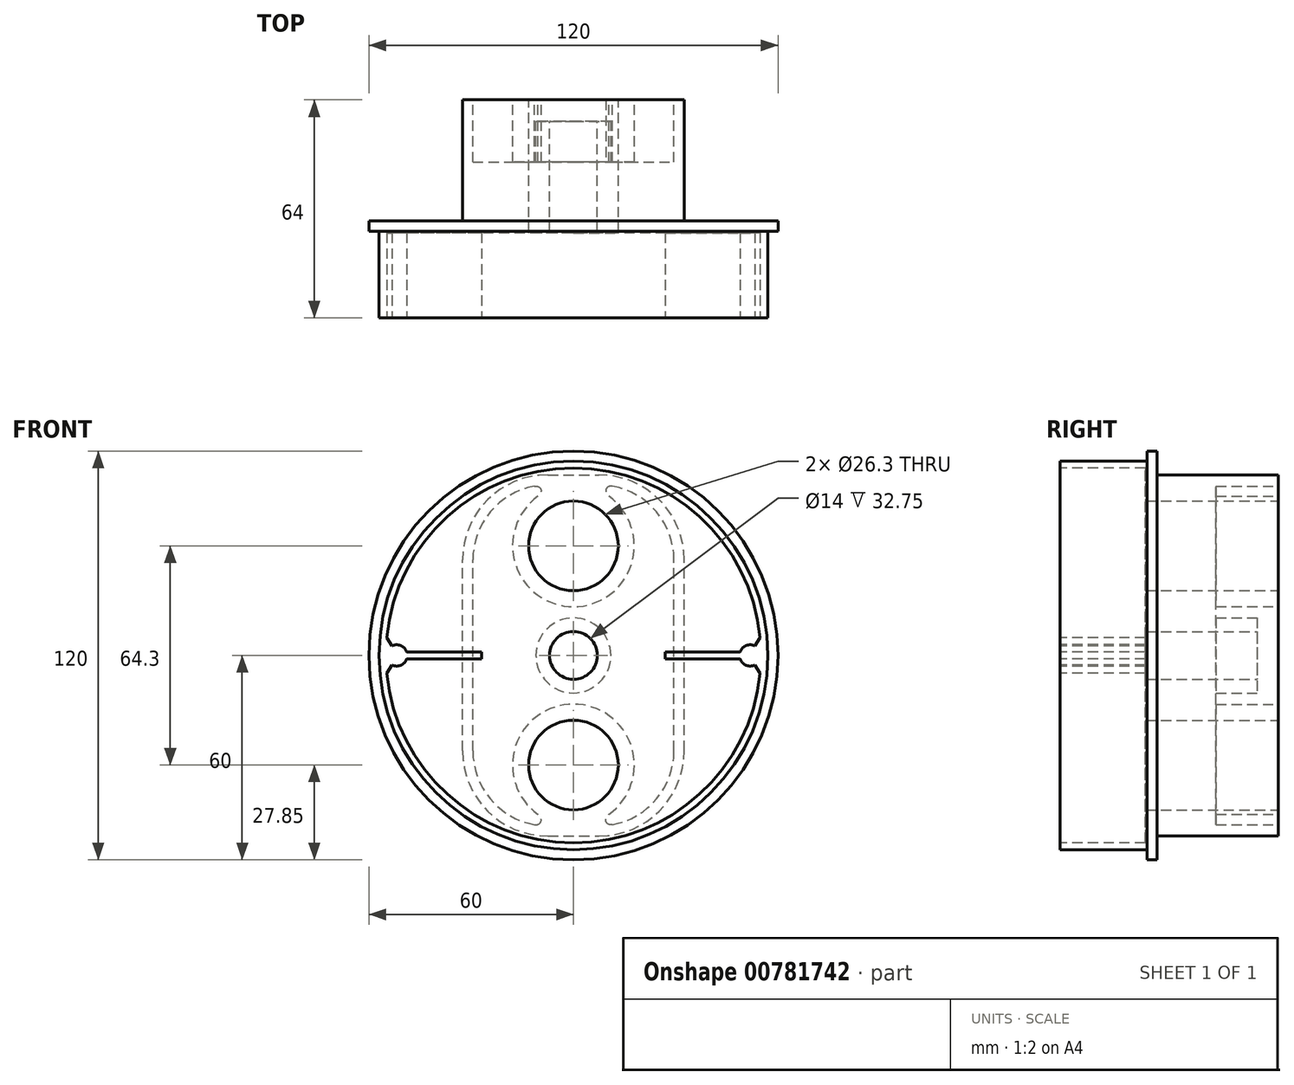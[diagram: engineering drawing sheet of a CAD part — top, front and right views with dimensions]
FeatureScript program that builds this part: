
annotation { "Feature Type Name" : "Feature", "Feature Type Description" : "" }
export const myFeature = defineFeature(function(context is Context, id is Id, definition is map)
    precondition{}
    {
        {
            var Q0;
            Q0=qCreatedBy(makeId("Front.planeOp"),FACE);
            var sketch = newSketch(context, id + "F0", { "sketchPlane" : qUnion([Q0])});
            skLineSegment(sketch, "E0.bottom", {"start": v(-7.5, -53) * mm, "end": v(7.5, -53) * mm});
            skLineSegment(sketch, "E0.top", {"start": v(-7.5, 53) * mm, "end": v(7.5, 53) * mm});
            skLineSegment(sketch, "E0.left", {"start": v(-32.5, -28) * mm, "end": v(-32.5, 28) * mm});
            skLineSegment(sketch, "E0.right", {"start": v(32.5, -28) * mm, "end": v(32.5, 28) * mm});
            skPoint(sketch, "E0.middle", {"position": v(0, 0) * mm});
            skPoint(sketch, "E1.visualSharp", {"position": v(32.5, 53) * mm});
            skArc(sketch, "E1.filletArc", {"start": v(32.5, 28) * mm, "mid": v(25.18, 45.68) * mm, "end": v(7.5, 53) * mm});
            skPoint(sketch, "E2.visualSharp", {"position": v(-32.5, 53) * mm});
            skArc(sketch, "E2.filletArc", {"start": v(-7.5, 53) * mm, "mid": v(-25.18, 45.68) * mm, "end": v(-32.5, 28) * mm});
            skPoint(sketch, "E3.visualSharp", {"position": v(32.5, -53) * mm});
            skArc(sketch, "E3.filletArc", {"start": v(7.5, -53) * mm, "mid": v(25.18, -45.68) * mm, "end": v(32.5, -28) * mm});
            skPoint(sketch, "E4.visualSharp", {"position": v(-32.5, -53) * mm});
            skArc(sketch, "E4.filletArc", {"start": v(-32.5, -28) * mm, "mid": v(-25.18, -45.68) * mm, "end": v(-7.5, -53) * mm});
            skSolve(sketch);
        }
        {
            var Q0;
            Q0 = qSketchRegion(id + "F0", true);
            extrude(context, id + "F1", {"entities" : qUnion([Q0]), "depth" : 64 * mm, "offsetDistance" : 25 * mm});
        }
        {
            var Q0;
            Q0=makeQuery(id+"F1.opExtrude","CAP_FACE",FACE,{"disambiguationData":[OSD([sQuery(id+"F0.wireOp",EDGE,"E0.bottom"),sQuery(id+"F0.wireOp",EDGE,"E0.top"),sQuery(id+"F0.wireOp",EDGE,"E0.left"),sQuery(id+"F0.wireOp",EDGE,"E0.right"),sQuery(id+"F0.wireOp",EDGE,"E1.filletArc"),sQuery(id+"F0.wireOp",EDGE,"E2.filletArc"),sQuery(id+"F0.wireOp",EDGE,"E3.filletArc"),sQuery(id+"F0.wireOp",EDGE,"E4.filletArc")])],"isStart":false});
            var sketch = newSketch(context, id + "F2", { "sketchPlane" : qUnion([Q0])});
            skCircle(sketch, "E5", {"center": v(0, 0) * mm, "radius": 60 * mm});
            skSolve(sketch);
        }
        {
            var Q0;
            Q0 = qSketchRegion(id + "F2", true);
            extrude(context, id + "F3", {"entities" : qUnion([Q0]), "operationType" : NewBodyOperationType.ADD, "oppositeDirection" : true, "depth" : 28.5 * mm, "offsetDistance" : 25 * mm});
        }
        {
            var Q0;
            Q0=makeQuery(id+"F3.boolean.opBoolean","MERGE",FACE,{"derivedFrom":[makeQuery(id+"F1.opExtrude","CAP_FACE",FACE,{"disambiguationData":[OSD([sQuery(id+"F0.wireOp",EDGE,"E0.bottom"),sQuery(id+"F0.wireOp",EDGE,"E0.top"),sQuery(id+"F0.wireOp",EDGE,"E0.left"),sQuery(id+"F0.wireOp",EDGE,"E0.right"),sQuery(id+"F0.wireOp",EDGE,"E1.filletArc"),sQuery(id+"F0.wireOp",EDGE,"E2.filletArc"),sQuery(id+"F0.wireOp",EDGE,"E3.filletArc"),sQuery(id+"F0.wireOp",EDGE,"E4.filletArc")])],"isStart":false}),makeQuery(id+"F3.opExtrude","CAP_FACE",FACE,{"disambiguationData":[OSD([sQuery(id+"F2.wireOp",EDGE,"E5")])],"isStart":true})]});
            var sketch = newSketch(context, id + "F4", { "sketchPlane" : qUnion([Q0])});
            skCircle(sketch, "E6", {"center": v(0, 0) * mm, "radius": 57 * mm});
            skSolve(sketch);
        }
        {
            var Q0;
            Q0=makeQuery(id+"F4.imprint","IMPRINT",FACE,{"disambiguationData":[TD([[makeQuery(id+"F4.imprint","IMPRINT",EDGE,{"derivedFrom":sQuery(id+"F4.wireOp",EDGE,"E6")}),-1.0]])]});
            extrude(context, id + "F5", {"entities" : qUnion([Q0]), "operationType" : NewBodyOperationType.REMOVE, "oppositeDirection" : true, "depth" : 25.5 * mm, "offsetDistance" : 25 * mm});
        }
        {
            var Q0;
            Q0=makeQuery(id+"F1.opExtrude","CAP_FACE",FACE,{"disambiguationData":[OSD([sQuery(id+"F0.wireOp",EDGE,"E0.bottom"),sQuery(id+"F0.wireOp",EDGE,"E0.top"),sQuery(id+"F0.wireOp",EDGE,"E0.left"),sQuery(id+"F0.wireOp",EDGE,"E0.right"),sQuery(id+"F0.wireOp",EDGE,"E1.filletArc"),sQuery(id+"F0.wireOp",EDGE,"E2.filletArc"),sQuery(id+"F0.wireOp",EDGE,"E3.filletArc"),sQuery(id+"F0.wireOp",EDGE,"E4.filletArc")])],"isStart":true});
            var sketch = newSketch(context, id + "F6", { "sketchPlane" : qUnion([Q0])});
            skCircle(sketch, "E7", {"center": v(0, 32.15) * mm, "radius": 17.85 * mm});
            skLineSegment(sketch, "E8", {"start": v(-65.9, 0) * mm, "end": v(78.7, 0) * mm, "construction": true});
            skLineSegment(sketch, "E9", {"start": v(0, 0) * mm, "end": v(0, 73.33) * mm, "construction": true});
            skLineSegment(sketch, "E10.0", {"start": v(7.5, 50) * mm, "end": v(-7.5, 50) * mm});
            skArc(sketch, "E10.1", {"start": v(-29.5, 28) * mm, "mid": v(-23.06, 43.56) * mm, "end": v(-7.5, 50) * mm});
            skArc(sketch, "E10.2", {"start": v(7.5, 50) * mm, "mid": v(23.06, 43.56) * mm, "end": v(29.5, 28) * mm});
            skLineSegment(sketch, "E10.3", {"start": v(-29.5, -28) * mm, "end": v(-29.5, 28) * mm});
            skLineSegment(sketch, "E10.4", {"start": v(29.5, -28) * mm, "end": v(29.5, 28) * mm});
            skArc(sketch, "E10.5", {"start": v(29.5, -28) * mm, "mid": v(23.06, -43.56) * mm, "end": v(7.5, -50) * mm});
            skLineSegment(sketch, "E10.6", {"start": v(7.5, -50) * mm, "end": v(-7.5, -50) * mm});
            skArc(sketch, "E10.7", {"start": v(-7.5, -50) * mm, "mid": v(-23.06, -43.56) * mm, "end": v(-29.5, -28) * mm});
            skFitSpline(sketch, "E11", {"points": [v(11.42, 49.65) * mm, v(10.96, 46.24) * mm], "startDerivative": vector(-5.62, 0.77) * mm, "endDerivative": vector(7.76, -5.02) * mm});
            skFitSpline(sketch, "E12.MirrorCS", {"points": [v(-11.42, 49.65) * mm, v(-10.96, 46.24) * mm], "startDerivative": vector(5.62, 0.77) * mm, "endDerivative": vector(-7.76, -5.02) * mm});
            skCircle(sketch, "E13.MirrorC", {"center": v(0, -32.15) * mm, "radius": 17.85 * mm});
            skFitSpline(sketch, "E14.MirrorCS", {"points": [v(11.42, -49.65) * mm, v(10.96, -46.24) * mm], "startDerivative": vector(-5.62, -0.77) * mm, "endDerivative": vector(7.76, 5.02) * mm});
            skFitSpline(sketch, "E15.MirrorCS", {"points": [v(-11.42, -49.65) * mm, v(-10.96, -46.24) * mm], "startDerivative": vector(5.62, -0.77) * mm, "endDerivative": vector(-7.76, 5.02) * mm});
            skSolve(sketch);
        }
        {
            var Q0;
            {var subQ9=sQuery(id+"F6.wireOp",EDGE,"E10.3");Q0=makeQuery(id+"F6.imprint","IMPRINT",FACE,{"disambiguationData":[TD([[makeQuery(id+"F6.imprint","IMPRINT",EDGE,{"derivedFrom":subQ9}),-1.0]])]});}
            extrude(context, id + "F7", {"entities" : qUnion([Q0]), "operationType" : NewBodyOperationType.REMOVE, "oppositeDirection" : true, "depth" : 6.25 * mm, "offsetDistance" : 25 * mm});
        }
        {
            var Q0;
            Q0=makeQuery(id+"F1.opExtrude","CAP_FACE",FACE,{"disambiguationData":[OSD([sQuery(id+"F0.wireOp",EDGE,"E0.bottom"),sQuery(id+"F0.wireOp",EDGE,"E0.top"),sQuery(id+"F0.wireOp",EDGE,"E0.left"),sQuery(id+"F0.wireOp",EDGE,"E0.right"),sQuery(id+"F0.wireOp",EDGE,"E1.filletArc"),sQuery(id+"F0.wireOp",EDGE,"E2.filletArc"),sQuery(id+"F0.wireOp",EDGE,"E3.filletArc"),sQuery(id+"F0.wireOp",EDGE,"E4.filletArc")])],"isStart":true});
            var sketch = newSketch(context, id + "F8", { "sketchPlane" : qUnion([Q0])});
            skCircle(sketch, "E16", {"center": v(0, 32.15) * mm, "radius": 13.15 * mm});
            skLineSegment(sketch, "E17", {"start": v(54.2, 0) * mm, "end": v(-66.34, 0) * mm, "construction": true});
            skCircle(sketch, "E18.MirrorC", {"center": v(0, -32.15) * mm, "radius": 13.15 * mm});
            skSolve(sketch);
        }
        {
            var Q0;
            Q0 = qSketchRegion(id + "F8", true);
            extrude(context, id + "F9", {"entities" : qUnion([Q0]), "operationType" : NewBodyOperationType.REMOVE, "endBound" : BoundingType.THROUGH_ALL, "oppositeDirection" : true, "depth" : 25 * mm, "offsetDistance" : 25 * mm});
        }
        {
            var Q0;
            Q0=makeQuery(id+"F7.boolean.opBoolean","COPY",FACE,{"derivedFrom":makeQuery(id+"F7.opExtrude","CAP_FACE",FACE,{"disambiguationData":[OSD([sQuery(id+"F6.wireOp",EDGE,"cfc4fd5c-9e0e-4e43-b49a-5f67deb5fad3.0"),sQuery(id+"F6.wireOp",EDGE,"cfc4fd5c-9e0e-4e43-b49a-5f67deb5fad3.1"),sQuery(id+"F6.wireOp",EDGE,"cfc4fd5c-9e0e-4e43-b49a-5f67deb5fad3.3"),sQuery(id+"F6.wireOp",EDGE,"cfc4fd5c-9e0e-4e43-b49a-5f67deb5fad3.4"),sQuery(id+"F6.wireOp",EDGE,"cfc4fd5c-9e0e-4e43-b49a-5f67deb5fad3.5"),sQuery(id+"F6.wireOp",EDGE,"cfc4fd5c-9e0e-4e43-b49a-5f67deb5fad3.6"),sQuery(id+"F6.wireOp",EDGE,"E7"),sQuery(id+"F6.wireOp",EDGE,"cb34a09b-d966-4f87-b14f-0af1bd5756a2"),sQuery(id+"F6.wireOp",EDGE,"da72c8c9-aecc-4077-a5c9-0ccf4ffb46970.MirrorCS"),sQuery(id+"F6.wireOp",EDGE,"0dd2ac59-9375-437e-9dff-d9fa0eae28960.MirrorC"),sQuery(id+"F6.wireOp",EDGE,"29a003be-6f31-446f-a0a1-0094011e53fc0.MirrorCS"),sQuery(id+"F6.wireOp",EDGE,"5bbbd694-d7a1-43b7-8784-b86b15c2be660.MirrorCS")])],"isStart":false})});
            var sketch = newSketch(context, id + "F10", { "sketchPlane" : qUnion([Q0])});
            skCircle(sketch, "E19", {"center": v(0, 0) * mm, "radius": 11 * mm});
            skSolve(sketch);
        }
        {
            var Q0;
            Q0=makeQuery(id+"F10.imprint","IMPRINT",FACE,{"disambiguationData":[TD([[makeQuery(id+"F10.imprint","IMPRINT",EDGE,{"derivedFrom":sQuery(id+"F10.wireOp",EDGE,"E19")}),-1.0]])]});
            extrude(context, id + "F11", {"entities" : qUnion([Q0]), "operationType" : NewBodyOperationType.REMOVE, "oppositeDirection" : true, "depth" : 12 * mm, "offsetDistance" : 25 * mm});
        }
        {
            var Q0;
            Q0=makeQuery(id+"F3.boolean.opBoolean","MERGE",FACE,{"derivedFrom":[makeQuery(id+"F1.opExtrude","CAP_FACE",FACE,{"disambiguationData":[OSD([sQuery(id+"F0.wireOp",EDGE,"E0.bottom"),sQuery(id+"F0.wireOp",EDGE,"E0.top"),sQuery(id+"F0.wireOp",EDGE,"E0.left"),sQuery(id+"F0.wireOp",EDGE,"E0.right"),sQuery(id+"F0.wireOp",EDGE,"E1.filletArc"),sQuery(id+"F0.wireOp",EDGE,"E2.filletArc"),sQuery(id+"F0.wireOp",EDGE,"E3.filletArc"),sQuery(id+"F0.wireOp",EDGE,"E4.filletArc")])],"isStart":false}),makeQuery(id+"F3.opExtrude","CAP_FACE",FACE,{"disambiguationData":[OSD([sQuery(id+"F2.wireOp",EDGE,"E5")])],"isStart":true})]});
            var sketch = newSketch(context, id + "F12", { "sketchPlane" : qUnion([Q0])});
            skCircle(sketch, "E20", {"center": v(-51.87, 0) * mm, "radius": 3.12 * mm});
            skLineSegment(sketch, "E21.bottom", {"start": v(-26.91, 1) * mm, "end": v(-48.91, 1) * mm});
            skLineSegment(sketch, "E21.top", {"start": v(-26.91, -1) * mm, "end": v(-48.91, -1) * mm});
            skLineSegment(sketch, "E21.left", {"start": v(-26.91, 1) * mm, "end": v(-26.91, -1) * mm});
            skPoint(sketch, "E21.middle", {"position": v(-37.91, 0) * mm});
            skCircle(sketch, "E22.0", {"center": v(0, 0) * mm, "radius": 55 * mm});
            skLineSegment(sketch, "E23", {"start": v(-54.75, 5.22) * mm, "end": v(-53.16, 2.85) * mm});
            skLineSegment(sketch, "E24", {"start": v(-51.87, 0) * mm, "end": v(-56.06, 0) * mm, "construction": true});
            skLineSegment(sketch, "E25.MirrorCS", {"start": v(-54.75, -5.22) * mm, "end": v(-53.16, -2.85) * mm});
            skLineSegment(sketch, "E26", {"start": v(0, 7.1) * mm, "end": v(0, -8.55) * mm, "construction": true});
            skLineSegment(sketch, "E27.MirrorCS", {"start": v(26.91, 1) * mm, "end": v(26.91, -1) * mm});
            skLineSegment(sketch, "E28.MirrorCS", {"start": v(26.91, 1) * mm, "end": v(48.91, 1) * mm});
            skLineSegment(sketch, "E29.MirrorCS", {"start": v(26.91, -1) * mm, "end": v(48.91, -1) * mm});
            skCircle(sketch, "E30.MirrorC", {"center": v(51.87, 0) * mm, "radius": 3.12 * mm});
            skLineSegment(sketch, "E31.MirrorCS", {"start": v(54.75, 5.22) * mm, "end": v(53.16, 2.85) * mm});
            skLineSegment(sketch, "E32.MirrorCS", {"start": v(54.75, -5.22) * mm, "end": v(53.16, -2.85) * mm});
            skSolve(sketch);
        }
        {
            var Q0;
            {var subQ5=sQuery(id+"F12.wireOp",EDGE,"E21.bottom");Q0=makeQuery(id+"F12.imprint","IMPRINT",FACE,{"disambiguationData":[TD([[makeQuery(id+"F12.imprint","IMPRINT",EDGE,{"derivedFrom":subQ5}),-1.0]])]});}
            extrude(context, id + "F13", {"entities" : qUnion([Q0]), "operationType" : NewBodyOperationType.REMOVE, "oppositeDirection" : true, "depth" : 25 * mm, "offsetDistance" : 25 * mm});
        }
        {
            var Q0;
            Q0=makeQuery(id+"F7.boolean.opBoolean","COPY",FACE,{"derivedFrom":makeQuery(id+"F7.opExtrude","CAP_FACE",FACE,{"disambiguationData":[OSD([sQuery(id+"F6.wireOp",EDGE,"E7"),sQuery(id+"F6.wireOp",EDGE,"E10.1"),sQuery(id+"F6.wireOp",EDGE,"E10.2"),sQuery(id+"F6.wireOp",EDGE,"E10.3"),sQuery(id+"F6.wireOp",EDGE,"E10.4"),sQuery(id+"F6.wireOp",EDGE,"E10.5"),sQuery(id+"F6.wireOp",EDGE,"E10.7"),sQuery(id+"F6.wireOp",EDGE,"E11"),sQuery(id+"F6.wireOp",EDGE,"E12.MirrorCS"),sQuery(id+"F6.wireOp",EDGE,"E13.MirrorC"),sQuery(id+"F6.wireOp",EDGE,"E14.MirrorCS"),sQuery(id+"F6.wireOp",EDGE,"E15.MirrorCS")])],"isStart":false})});
            var sketch = newSketch(context, id + "F14", { "sketchPlane" : qUnion([Q0])});
            skCircle(sketch, "E33", {"center": v(0, 0) * mm, "radius": 7 * mm});
            skSolve(sketch);
        }
        {
            var Q0;
            Q0=makeQuery(id+"F14.imprint","IMPRINT",FACE,{"disambiguationData":[TD([[makeQuery(id+"F14.imprint","IMPRINT",EDGE,{"derivedFrom":sQuery(id+"F14.wireOp",EDGE,"E33")}),1.0]])]});
            extrude(context, id + "F15", {"entities" : qUnion([Q0]), "operationType" : NewBodyOperationType.REMOVE, "endBound" : BoundingType.THROUGH_ALL, "oppositeDirection" : true, "depth" : 25 * mm, "offsetDistance" : 25 * mm});
        }
    });
